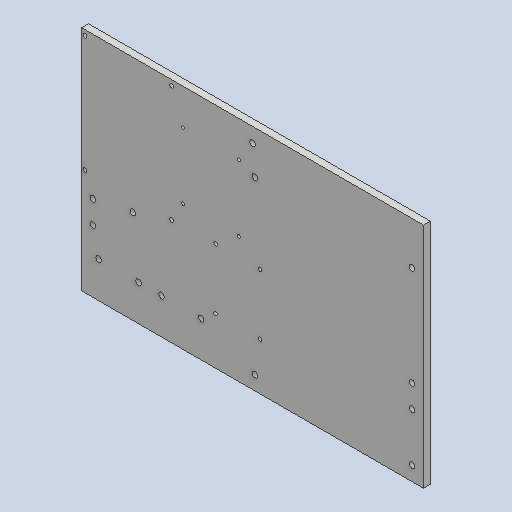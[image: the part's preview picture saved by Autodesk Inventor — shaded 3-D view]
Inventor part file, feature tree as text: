
AUTODESK INVENTOR PART (.ipt)
format: ipt  version: 2023 (Build 270158000, 158)  size: 144,384 bytes
history: native  units: mm
features: reference x26, other x13, extrude x2, sketch x2
ambient origin geometry x8: Origin, YZ Plane, XZ Plane, XY Plane, X Axis, Y Axis, Z Axis, Center Point
bodies: Solid1 (feature_tree)
feature tree (43):
  extrude  "Extrusion1"  Depth=200.0mm
  extrude  "Extrusion2"  Depth=300.0mm TaperAngle=0.0deg
  sketch  "Sketch1"  dims[d0=6.0mm d1=0.0mm d2=200.0mm]
  sketch  "Sketch2"  dims[d3=300.0mm d4=30.0mm d5=0.0mm]
  reference  "Reference1"
  reference  "Reference2"
  reference  "Reference3"
  reference  "Reference4"
  reference  "Reference5"
  reference  "Reference6"
  reference  "Reference7"
  reference  "Reference8"
  reference  "Reference9"
  reference  "Reference10"
  reference  "Reference11"
  reference  "Reference12"
  reference  "Reference13"
  reference  "Reference14"
  reference  "Reference15"
  reference  "Reference16"
  reference  "Reference17"
  reference  "Reference18"
  reference  "Reference19"
  reference  "Reference20"
  reference  "Reference21"
  reference  "Reference22"
  reference  "Reference23"
  reference  "Reference24"
  reference  "Reference25"
  reference  "Reference26"
  other  "<userpath>\OneDrive\ClawdDrive\Objet3D\3DPrinter\inventor\3DPrinterBeltCoreXY.iam"
  other  "3DPrinterBeltCoreXY.iam"
  other  "PSUBracketPowerConnector:1"
  other  "PSUBracket:1"
  other  "RelayBracket:2"
  other  "RelayBracket:1"
  other  "dc-dc SZBK07:1"
  other  "Raspberry Pi 4 Model B:1"
  other  "mks sgen l v2.0:1"
  other  "BracketControlPannel:1"
  other  "BracketControlPannel:2"
  other  "FanSpace:1"
  other  "FanSpace:2"
